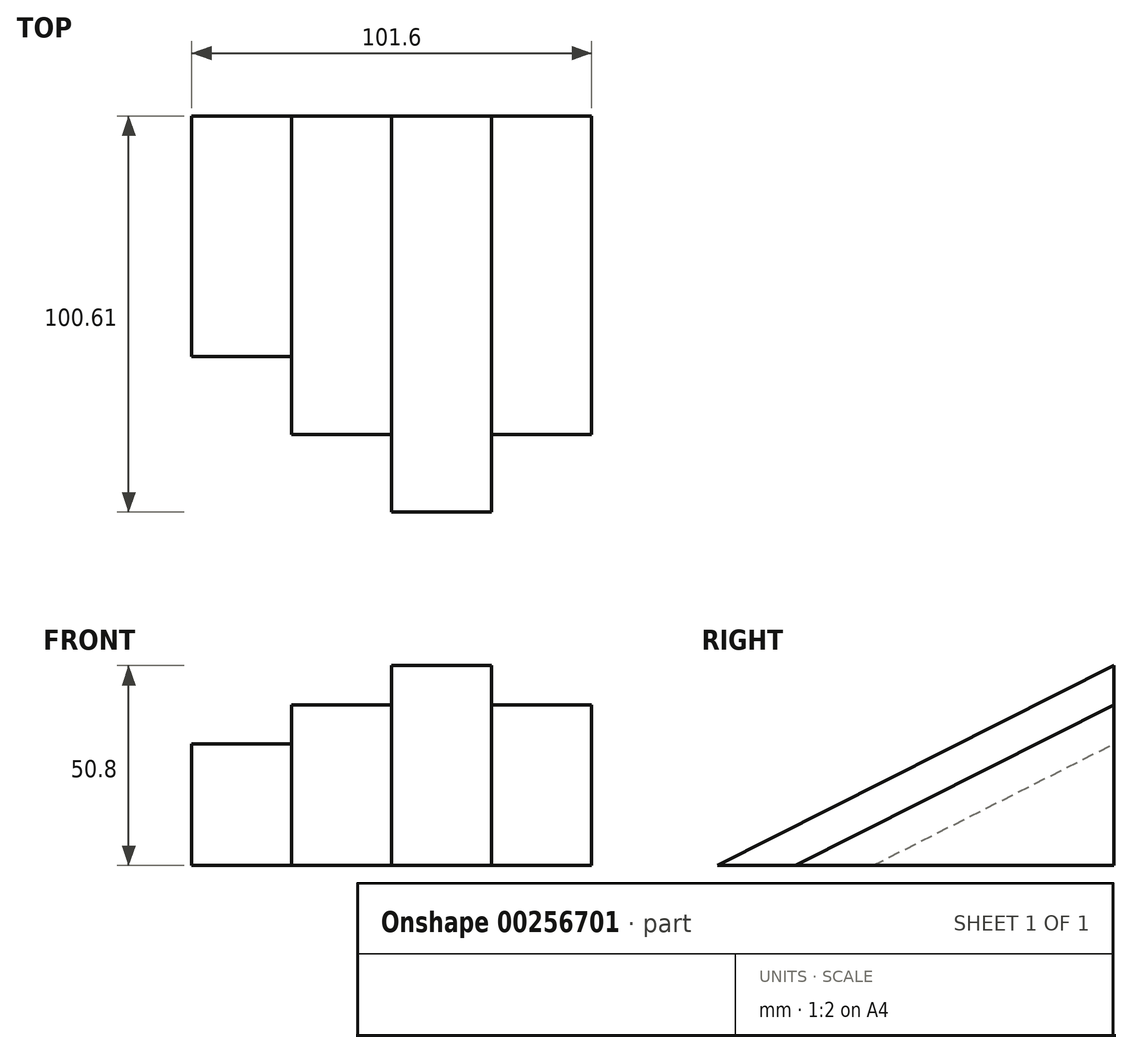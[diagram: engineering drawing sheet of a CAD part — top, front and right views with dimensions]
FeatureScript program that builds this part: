
annotation { "Feature Type Name" : "Feature", "Feature Type Description" : "" }
export const myFeature = defineFeature(function(context is Context, id is Id, definition is map)
    precondition{}
    {
        {
            var Q0;
            Q0=qCreatedBy(makeId("Right.planeOp"),FACE);
            var sketch = newSketch(context, id + "F0", { "sketchPlane" : qUnion([Q0])});
            skLineSegment(sketch, "E0", {"start": v(-45.81, 0) * mm, "end": v(30.39, 0) * mm});
            skLineSegment(sketch, "E1", {"start": v(54.8, 7) * mm, "end": v(54.8, 50.8) * mm});
            skLineSegment(sketch, "E2", {"start": v(54.8, 50.8) * mm, "end": v(-45.81, 0) * mm});
            skLineSegment(sketch, "E3", {"start": v(54.8, 7) * mm, "end": v(54.8, 0) * mm});
            skLineSegment(sketch, "E4", {"start": v(54.8, 0) * mm, "end": v(30.39, 0) * mm});
            skSolve(sketch);
        }
        {
            var Q0;
            Q0 = qSketchRegion(id + "F0", true);
            extrude(context, id + "F1", {"entities" : qUnion([Q0]), "oppositeDirection" : true, "depth" : 25.4 * mm});
        }
        {
            var Q0;
            Q0=makeQuery(id+"F1.opExtrude","CAP_FACE",FACE,{"disambiguationData":[OSD([sQuery(id+"F0.wireOp",EDGE,"E0"),sQuery(id+"F0.wireOp",EDGE,"JH4v1hcX-QNGI-gfvF-352M-g6sxYzJgDv42"),sQuery(id+"F0.wireOp",EDGE,"E1"),sQuery(id+"F0.wireOp",EDGE,"E2")])],"isStart":false});
            var sketch = newSketch(context, id + "F2", { "sketchPlane" : qUnion([Q0])});
            skPoint(sketch, "E5.endSnap0", {"position": v(10.3, 0) * mm});
            skPoint(sketch, "E6.orphan", {"position": v(45.81, 0) * mm});
            skPoint(sketch, "E7.end.orphan", {"position": v(-25.21, 0) * mm});
            skLineSegment(sketch, "E8", {"start": v(-54.8, 0) * mm, "end": v(32.35, 0) * mm});
            skLineSegment(sketch, "E9", {"start": v(-54.8, 40.84) * mm, "end": v(26.09, 0) * mm});
            skLineSegment(sketch, "E10", {"start": v(32.35, 0) * mm, "end": v(26.09, 0) * mm});
            skLineSegment(sketch, "E11", {"start": v(-54.8, 0) * mm, "end": v(-54.8, 40.84) * mm});
            skSolve(sketch);
        }
        {
            var Q0;
            Q0 = qSketchRegion(id + "F2", true);
            extrude(context, id + "F3", {"entities" : qUnion([Q0]), "operationType" : NewBodyOperationType.ADD, "depth" : 25.4 * mm});
        }
        {
            var Q0;
            Q0=makeQuery(id+"F3.opExtrude","CAP_FACE",FACE,{"disambiguationData":[OSD([sQuery(id+"F2.wireOp",EDGE,"E8"),sQuery(id+"F2.wireOp",EDGE,"E9"),sQuery(id+"F2.wireOp",EDGE,"E10"),sQuery(id+"F2.wireOp",EDGE,"E11")])],"isStart":false});
            var sketch = newSketch(context, id + "F4", { "sketchPlane" : qUnion([Q0])});
            skLineSegment(sketch, "E12", {"start": v(-34.97, 0) * mm, "end": v(6.36, 0) * mm});
            skLineSegment(sketch, "E13", {"start": v(6.36, 0) * mm, "end": v(-54.8, 30.88) * mm});
            skLineSegment(sketch, "E14", {"start": v(-54.8, 0) * mm, "end": v(-34.97, 0) * mm});
            skLineSegment(sketch, "E15", {"start": v(-54.8, 30.88) * mm, "end": v(-54.8, 0) * mm});
            skSolve(sketch);
        }
        {
            var Q0;
            Q0 = qSketchRegion(id + "F4", true);
            extrude(context, id + "F5", {"entities" : qUnion([Q0]), "operationType" : NewBodyOperationType.ADD, "depth" : 25.4 * mm});
        }
        {
            var Q0;
            Q0=makeQuery(id+"F1.opExtrude","CAP_FACE",FACE,{"disambiguationData":[OSD([sQuery(id+"F0.wireOp",EDGE,"E0"),sQuery(id+"F0.wireOp",EDGE,"JH4v1hcX-QNGI-gfvF-352M-g6sxYzJgDv42"),sQuery(id+"F0.wireOp",EDGE,"E1"),sQuery(id+"F0.wireOp",EDGE,"E2")])],"isStart":true});
            var sketch = newSketch(context, id + "F6", { "sketchPlane" : qUnion([Q0])});
            skLineSegment(sketch, "E16", {"start": v(-26.09, 0) * mm, "end": v(23.77, 0) * mm});
            skLineSegment(sketch, "E17", {"start": v(54.8, 40.84) * mm, "end": v(-26.09, 0) * mm});
            skLineSegment(sketch, "E18", {"start": v(54.8, 40.84) * mm, "end": v(54.8, 10.36) * mm});
            skLineSegment(sketch, "E19", {"start": v(54.8, 10.36) * mm, "end": v(54.8, 0) * mm});
            skLineSegment(sketch, "E20", {"start": v(54.8, 0) * mm, "end": v(23.77, 0) * mm});
            skSolve(sketch);
        }
        {
            var Q0;
            Q0 = qSketchRegion(id + "F6", true);
            extrude(context, id + "F7", {"entities" : qUnion([Q0]), "operationType" : NewBodyOperationType.ADD, "depth" : 25.4 * mm});
        }
        {
            var Q0;
            Q0=qCreatedBy(makeId("Right.planeOp"),FACE);
            cPlane(context, id + "F8", {"entities" : qUnion([Q0]), "cplaneType" : CPlaneType.OFFSET, "offset" : 84.33 * mm, "oppositeDirection" : true, "width" : 152.4 * mm, "height" : 152.4 * mm});
        }
    });
